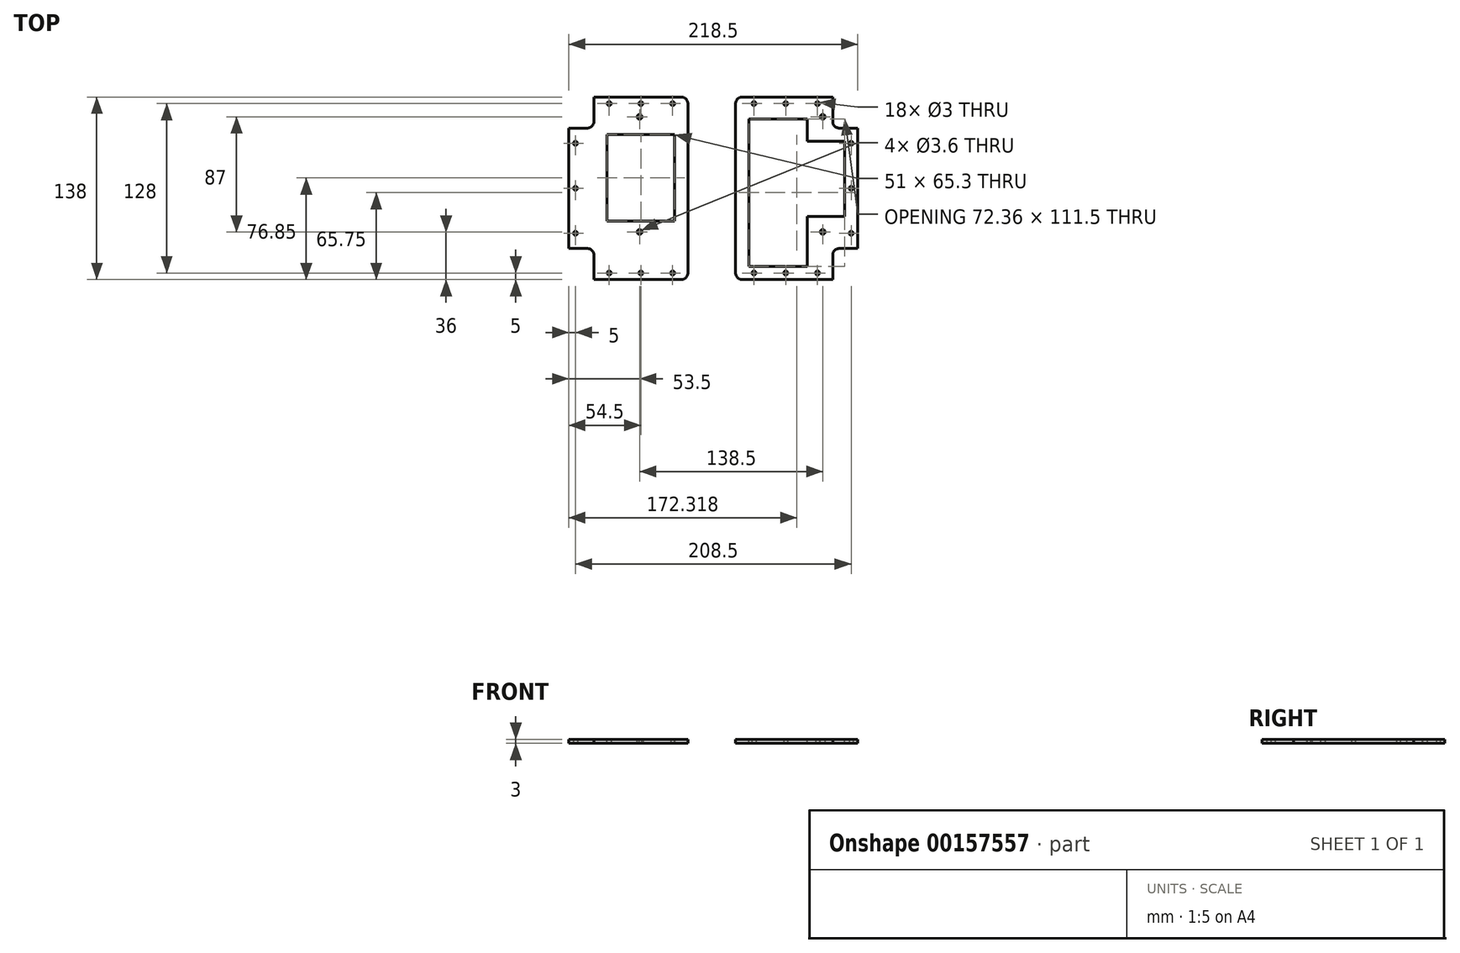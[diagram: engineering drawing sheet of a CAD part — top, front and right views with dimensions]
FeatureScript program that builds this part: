
annotation { "Feature Type Name" : "Feature", "Feature Type Description" : "" }
export const myFeature = defineFeature(function(context is Context, id is Id, definition is map)
    precondition{}
    {
        {
            var Q0;
            Q0=qCreatedBy(makeId("Top.planeOp"),FACE);
            var sketch = newSketch(context, id + "F0", { "sketchPlane" : qUnion([Q0])});
            skLineSegment(sketch, "E0.bottom", {"start": v(49.5, 64) * mm, "end": v(-49.5, 64) * mm, "construction": true});
            skLineSegment(sketch, "E0.top", {"start": v(49.5, -64) * mm, "end": v(-49.5, -64) * mm, "construction": true});
            skLineSegment(sketch, "E0.left", {"start": v(49.5, 64) * mm, "end": v(49.5, -64) * mm, "construction": true});
            skLineSegment(sketch, "E0.right", {"start": v(-49.5, 64) * mm, "end": v(-49.5, -64) * mm, "construction": true});
            skPoint(sketch, "E0.middle", {"position": v(0, 0) * mm});
            skCircle(sketch, "E1", {"center": v(-49.5, 0) * mm, "radius": 1.5 * mm});
            skCircle(sketch, "E2", {"center": v(-49.5, 34) * mm, "radius": 1.5 * mm});
            skCircle(sketch, "E3", {"center": v(-49.5, -34) * mm, "radius": 1.5 * mm});
            skCircle(sketch, "E4", {"center": v(-24, -64) * mm, "radius": 1.5 * mm});
            skCircle(sketch, "E5", {"center": v(0, -64) * mm, "radius": 1.5 * mm});
            skCircle(sketch, "E6", {"center": v(24, -64) * mm, "radius": 1.5 * mm});
            skCircle(sketch, "E7", {"center": v(0, 64) * mm, "radius": 1.5 * mm});
            skCircle(sketch, "E8", {"center": v(24, 64) * mm, "radius": 1.5 * mm});
            skCircle(sketch, "E9", {"center": v(-24, 64) * mm, "radius": 1.5 * mm});
            skLineSegment(sketch, "E10.bottom", {"start": v(-54.5, 69) * mm, "end": v(35.5, 69) * mm});
            skLineSegment(sketch, "E10.top", {"start": v(-54.5, -69) * mm, "end": v(35.5, -69) * mm});
            skLineSegment(sketch, "E10.left", {"start": v(-54.5, 69) * mm, "end": v(-54.5, -69) * mm});
            skLineSegment(sketch, "E10.right", {"start": v(35.5, 69) * mm, "end": v(35.5, -69) * mm});
            skLineSegment(sketch, "E11.bottom", {"start": v(60, 64) * mm, "end": v(159, 64) * mm, "construction": true});
            skLineSegment(sketch, "E11.top", {"start": v(60, -64) * mm, "end": v(159, -64) * mm, "construction": true});
            skLineSegment(sketch, "E11.left", {"start": v(60, 64) * mm, "end": v(60, -64) * mm, "construction": true});
            skLineSegment(sketch, "E11.right", {"start": v(159, 64) * mm, "end": v(159, -64) * mm, "construction": true});
            skCircle(sketch, "E12", {"center": v(85.5, 64) * mm, "radius": 1.5 * mm});
            skCircle(sketch, "E13", {"center": v(109.5, 64) * mm, "radius": 1.5 * mm});
            skCircle(sketch, "E14", {"center": v(133.5, 64) * mm, "radius": 1.5 * mm});
            skCircle(sketch, "E15", {"center": v(109.5, -64) * mm, "radius": 1.5 * mm});
            skCircle(sketch, "E16", {"center": v(133.5, -64) * mm, "radius": 1.5 * mm});
            skCircle(sketch, "E17", {"center": v(85.5, -64) * mm, "radius": 1.5 * mm});
            skCircle(sketch, "E18", {"center": v(159, 34) * mm, "radius": 1.5 * mm});
            skCircle(sketch, "E19", {"center": v(159, 0) * mm, "radius": 1.5 * mm});
            skCircle(sketch, "E20", {"center": v(159, -34) * mm, "radius": 1.5 * mm});
            skLineSegment(sketch, "E21.bottom", {"start": v(71.64, 69) * mm, "end": v(164, 69) * mm});
            skLineSegment(sketch, "E21.top", {"start": v(71.64, -69) * mm, "end": v(164, -69) * mm});
            skLineSegment(sketch, "E21.left", {"start": v(71.64, 69) * mm, "end": v(71.64, -69) * mm});
            skLineSegment(sketch, "E21.right", {"start": v(164, 69) * mm, "end": v(164, -69) * mm});
            skSolve(sketch);
        }
        {
            var Q0;
            Q0=makeQuery(id+"F0.imprint","IMPRINT",FACE,{"disambiguationData":[TD([[makeQuery(id+"F0.imprint","IMPRINT",EDGE,{"derivedFrom":sQuery(id+"F0.wireOp",EDGE,"E1")}),-1.0]])]});
            var Q1;
            Q1=makeQuery(id+"F0.imprint","IMPRINT",FACE,{"disambiguationData":[TD([[makeQuery(id+"F0.imprint","IMPRINT",EDGE,{"derivedFrom":sQuery(id+"F0.wireOp",EDGE,"E12")}),-1.0]])]});
            extrude(context, id + "F1", {"entities" : qUnion([Q0, Q1]), "depth" : 3 * mm});
        }
        {
            var Q0;
            Q0=makeQuery(id+"F1.opExtrude","CAP_FACE",FACE,{"disambiguationData":[OSD([sQuery(id+"F0.wireOp",EDGE,"E1"),sQuery(id+"F0.wireOp",EDGE,"E2"),sQuery(id+"F0.wireOp",EDGE,"E3"),sQuery(id+"F0.wireOp",EDGE,"E4"),sQuery(id+"F0.wireOp",EDGE,"E5"),sQuery(id+"F0.wireOp",EDGE,"E6"),sQuery(id+"F0.wireOp",EDGE,"E7"),sQuery(id+"F0.wireOp",EDGE,"E8"),sQuery(id+"F0.wireOp",EDGE,"E9"),sQuery(id+"F0.wireOp",EDGE,"E10.bottom"),sQuery(id+"F0.wireOp",EDGE,"E10.top"),sQuery(id+"F0.wireOp",EDGE,"E10.left"),sQuery(id+"F0.wireOp",EDGE,"E10.right")])],"isStart":false});
            var sketch = newSketch(context, id + "F2", { "sketchPlane" : qUnion([Q0])});
            skLineSegment(sketch, "E22.bottom", {"start": v(-57.57, 71.82) * mm, "end": v(-35.5, 71.82) * mm});
            skLineSegment(sketch, "E22.top", {"start": v(-57.57, 45.5) * mm, "end": v(-35.5, 45.5) * mm});
            skLineSegment(sketch, "E22.left", {"start": v(-57.57, 71.82) * mm, "end": v(-57.57, 45.5) * mm});
            skLineSegment(sketch, "E22.right", {"start": v(-35.5, 71.82) * mm, "end": v(-35.5, 45.5) * mm});
            skLineSegment(sketch, "E23.bottom", {"start": v(-60.22, -45.5) * mm, "end": v(-35.5, -45.5) * mm});
            skLineSegment(sketch, "E23.top", {"start": v(-60.22, -76.77) * mm, "end": v(-35.5, -76.77) * mm});
            skLineSegment(sketch, "E23.left", {"start": v(-60.22, -45.5) * mm, "end": v(-60.22, -76.77) * mm});
            skLineSegment(sketch, "E23.right", {"start": v(-35.5, -45.5) * mm, "end": v(-35.5, -76.77) * mm});
            skSolve(sketch);
        }
        {
            var Q0;
            Q0=makeQuery(id+"F2.imprint","IMPRINT",FACE,{"disambiguationData":[TD([[makeQuery(id+"F2.imprint","IMPRINT",EDGE,{"derivedFrom":sQuery(id+"F2.wireOp",EDGE,"VDgyCrDu-SPCL-fZ3l-5v9R-33bLlP5n6OBU.bottom")}),-1.0]])]});
            var Q1;
            {var subQ0=sQuery(id+"F2.wireOp",EDGE,"E22.right");var subQ1=sQuery(id+"F2.wireOp",EDGE,"E22.top");var subQ2=makeQuery(id+"F2.imprint","INTERSECT",VERTEX,{"derivedFrom":[subQ1,subQ0]});Q1=makeQuery(id+"F2.imprint","IMPRINT",FACE,{"disambiguationData":[TD([[makeQuery(id+"F2.imprint","IMPRINT",EDGE,{"disambiguationData":[TD([[subQ2,1.0]])],"derivedFrom":subQ1}),1.0]])]});}
            var Q2;
            {var subQ0=sQuery(id+"F2.wireOp",EDGE,"E23.right");var subQ1=sQuery(id+"F2.wireOp",EDGE,"E23.bottom");var subQ2=makeQuery(id+"F2.imprint","INTERSECT",VERTEX,{"derivedFrom":[subQ1,subQ0]});Q2=makeQuery(id+"F2.imprint","IMPRINT",FACE,{"disambiguationData":[TD([[makeQuery(id+"F2.imprint","IMPRINT",EDGE,{"disambiguationData":[TD([[subQ2,1.0]])],"derivedFrom":subQ1}),-1.0]])]});}
            extrude(context, id + "F3", {"entities" : qUnion([Q0, Q1, Q2]), "operationType" : NewBodyOperationType.REMOVE, "oppositeDirection" : true, "depth" : 25 * mm});
        }
        {
            var Q0;
            Q0=makeQuery(id+"F1.opExtrude","CAP_FACE",FACE,{"disambiguationData":[OSD([sQuery(id+"F0.wireOp",EDGE,"E12"),sQuery(id+"F0.wireOp",EDGE,"E13"),sQuery(id+"F0.wireOp",EDGE,"E14"),sQuery(id+"F0.wireOp",EDGE,"E15"),sQuery(id+"F0.wireOp",EDGE,"E16"),sQuery(id+"F0.wireOp",EDGE,"E17"),sQuery(id+"F0.wireOp",EDGE,"E18"),sQuery(id+"F0.wireOp",EDGE,"E19"),sQuery(id+"F0.wireOp",EDGE,"E20"),sQuery(id+"F0.wireOp",EDGE,"E21.bottom"),sQuery(id+"F0.wireOp",EDGE,"E21.top"),sQuery(id+"F0.wireOp",EDGE,"E21.left"),sQuery(id+"F0.wireOp",EDGE,"E21.right")])],"isStart":false});
            var sketch = newSketch(context, id + "F4", { "sketchPlane" : qUnion([Q0])});
            skLineSegment(sketch, "E24.bottom", {"start": v(145, 79.76) * mm, "end": v(176.38, 79.76) * mm});
            skLineSegment(sketch, "E24.top", {"start": v(145, 45.5) * mm, "end": v(176.38, 45.5) * mm});
            skLineSegment(sketch, "E24.left", {"start": v(145, 79.76) * mm, "end": v(145, 45.5) * mm});
            skLineSegment(sketch, "E24.right", {"start": v(176.38, 79.76) * mm, "end": v(176.38, 45.5) * mm});
            skLineSegment(sketch, "E25.bottom", {"start": v(145, -45.5) * mm, "end": v(181.26, -45.5) * mm});
            skLineSegment(sketch, "E25.top", {"start": v(145, -79.2) * mm, "end": v(181.26, -79.2) * mm});
            skLineSegment(sketch, "E25.left", {"start": v(145, -45.5) * mm, "end": v(145, -79.2) * mm});
            skLineSegment(sketch, "E25.right", {"start": v(181.26, -45.5) * mm, "end": v(181.26, -79.2) * mm});
            skSolve(sketch);
        }
        {
            var Q0;
            {var subQ0=sQuery(id+"F4.wireOp",EDGE,"E24.left");var subQ1=sQuery(id+"F4.wireOp",EDGE,"E24.top");var subQ2=makeQuery(id+"F4.imprint","INTERSECT",VERTEX,{"derivedFrom":[subQ1,subQ0]});Q0=makeQuery(id+"F4.imprint","IMPRINT",FACE,{"disambiguationData":[TD([[makeQuery(id+"F4.imprint","IMPRINT",EDGE,{"disambiguationData":[TD([[subQ2,-1.0]])],"derivedFrom":subQ1}),1.0]])]});}
            var Q1;
            {var subQ0=sQuery(id+"F4.wireOp",EDGE,"E25.left");var subQ1=sQuery(id+"F4.wireOp",EDGE,"E25.bottom");var subQ2=makeQuery(id+"F4.imprint","INTERSECT",VERTEX,{"derivedFrom":[subQ1,subQ0]});Q1=makeQuery(id+"F4.imprint","IMPRINT",FACE,{"disambiguationData":[TD([[makeQuery(id+"F4.imprint","IMPRINT",EDGE,{"disambiguationData":[TD([[subQ2,-1.0]])],"derivedFrom":subQ1}),-1.0]])]});}
            extrude(context, id + "F5", {"entities" : qUnion([Q0, Q1]), "operationType" : NewBodyOperationType.REMOVE, "oppositeDirection" : true, "depth" : 25 * mm});
        }
        {
            var Q0;
            Q0=makeQuery(id+"F3.boolean.opBoolean","COPY",EDGE,{"derivedFrom":makeQuery(id+"F3.opExtrude","SWEPT_EDGE",EDGE,{"disambiguationData":[OSD([sQuery(id+"F0.wireOp",EDGE,"E10.left"),sQuery(id+"F2.wireOp",EDGE,"E22.top")])]})});
            var Q1;
            Q1=makeQuery(id+"F3.boolean.opBoolean","COPY",EDGE,{"derivedFrom":makeQuery(id+"F3.opExtrude","SWEPT_EDGE",EDGE,{"disambiguationData":[OSD([sQuery(id+"F0.wireOp",EDGE,"E10.left"),sQuery(id+"F2.wireOp",EDGE,"E23.bottom")])]})});
            var Q2;
            Q2=makeQuery(id+"F3.boolean.opBoolean","COPY",EDGE,{"derivedFrom":makeQuery(id+"F3.opExtrude","SWEPT_EDGE",EDGE,{"disambiguationData":[OSD([sQuery(id+"F2.wireOp",EDGE,"E23.bottom"),sQuery(id+"F2.wireOp",EDGE,"E23.right")])]})});
            var Q3;
            Q3=makeQuery(id+"F3.boolean.opBoolean","COPY",EDGE,{"derivedFrom":makeQuery(id+"F3.opExtrude","SWEPT_EDGE",EDGE,{"disambiguationData":[OSD([sQuery(id+"F0.wireOp",EDGE,"E10.top"),sQuery(id+"F2.wireOp",EDGE,"E23.right")])]})});
            var Q4;
            Q4=makeQuery(id+"F1.opExtrude","SWEPT_EDGE",EDGE,{"disambiguationData":[OSD([sQuery(id+"F0.wireOp",EDGE,"E10.top"),sQuery(id+"F0.wireOp",EDGE,"E10.right")])]});
            var Q5;
            Q5=makeQuery(id+"F1.opExtrude","SWEPT_EDGE",EDGE,{"disambiguationData":[OSD([sQuery(id+"F0.wireOp",EDGE,"E10.bottom"),sQuery(id+"F0.wireOp",EDGE,"E10.right")])]});
            var Q6;
            Q6=makeQuery(id+"F3.boolean.opBoolean","COPY",EDGE,{"derivedFrom":makeQuery(id+"F3.opExtrude","SWEPT_EDGE",EDGE,{"disambiguationData":[OSD([sQuery(id+"F0.wireOp",EDGE,"E10.bottom"),sQuery(id+"F2.wireOp",EDGE,"E22.right")])]})});
            var Q7;
            Q7=makeQuery(id+"F3.boolean.opBoolean","COPY",EDGE,{"derivedFrom":makeQuery(id+"F3.opExtrude","SWEPT_EDGE",EDGE,{"disambiguationData":[OSD([sQuery(id+"F2.wireOp",EDGE,"E22.top"),sQuery(id+"F2.wireOp",EDGE,"E22.right")])]})});
            var Q8;
            Q8=makeQuery(id+"F3.boolean.opBoolean","COPY",EDGE,{"derivedFrom":makeQuery(id+"F3.opExtrude","SWEPT_EDGE",EDGE,{"disambiguationData":[OSD([sQuery(id+"F2.wireOp",EDGE,"VDgyCrDu-SPCL-fZ3l-5v9R-33bLlP5n6OBU.bottom"),sQuery(id+"F2.wireOp",EDGE,"VDgyCrDu-SPCL-fZ3l-5v9R-33bLlP5n6OBU.left")])]})});
            var Q9;
            Q9=makeQuery(id+"F3.boolean.opBoolean","COPY",EDGE,{"derivedFrom":makeQuery(id+"F3.opExtrude","SWEPT_EDGE",EDGE,{"disambiguationData":[OSD([sQuery(id+"F2.wireOp",EDGE,"VDgyCrDu-SPCL-fZ3l-5v9R-33bLlP5n6OBU.bottom"),sQuery(id+"F2.wireOp",EDGE,"VDgyCrDu-SPCL-fZ3l-5v9R-33bLlP5n6OBU.right")])]})});
            var Q10;
            Q10=makeQuery(id+"F3.boolean.opBoolean","COPY",EDGE,{"derivedFrom":makeQuery(id+"F3.opExtrude","SWEPT_EDGE",EDGE,{"disambiguationData":[OSD([sQuery(id+"F2.wireOp",EDGE,"VDgyCrDu-SPCL-fZ3l-5v9R-33bLlP5n6OBU.top"),sQuery(id+"F2.wireOp",EDGE,"VDgyCrDu-SPCL-fZ3l-5v9R-33bLlP5n6OBU.right")])]})});
            var Q11;
            Q11=makeQuery(id+"F3.boolean.opBoolean","COPY",EDGE,{"derivedFrom":makeQuery(id+"F3.opExtrude","SWEPT_EDGE",EDGE,{"disambiguationData":[OSD([sQuery(id+"F2.wireOp",EDGE,"VDgyCrDu-SPCL-fZ3l-5v9R-33bLlP5n6OBU.top"),sQuery(id+"F2.wireOp",EDGE,"VDgyCrDu-SPCL-fZ3l-5v9R-33bLlP5n6OBU.left")])]})});
            var Q12;
            Q12=makeQuery(id+"F1.opExtrude","SWEPT_EDGE",EDGE,{"disambiguationData":[OSD([sQuery(id+"F0.wireOp",EDGE,"E21.bottom"),sQuery(id+"F0.wireOp",EDGE,"E21.left")])]});
            var Q13;
            Q13=makeQuery(id+"F5.boolean.opBoolean","COPY",EDGE,{"derivedFrom":makeQuery(id+"F5.opExtrude","SWEPT_EDGE",EDGE,{"disambiguationData":[OSD([sQuery(id+"F0.wireOp",EDGE,"E21.bottom"),sQuery(id+"F4.wireOp",EDGE,"E24.left")])]})});
            var Q14;
            Q14=makeQuery(id+"F5.boolean.opBoolean","COPY",EDGE,{"derivedFrom":makeQuery(id+"F5.opExtrude","SWEPT_EDGE",EDGE,{"disambiguationData":[OSD([sQuery(id+"F4.wireOp",EDGE,"E24.top"),sQuery(id+"F4.wireOp",EDGE,"E24.left")])]})});
            var Q15;
            Q15=makeQuery(id+"F5.boolean.opBoolean","COPY",EDGE,{"derivedFrom":makeQuery(id+"F5.opExtrude","SWEPT_EDGE",EDGE,{"disambiguationData":[OSD([sQuery(id+"F0.wireOp",EDGE,"E21.right"),sQuery(id+"F4.wireOp",EDGE,"E24.top")])]})});
            var Q16;
            Q16=makeQuery(id+"F5.boolean.opBoolean","COPY",EDGE,{"derivedFrom":makeQuery(id+"F5.opExtrude","SWEPT_EDGE",EDGE,{"disambiguationData":[OSD([sQuery(id+"F0.wireOp",EDGE,"E21.right"),sQuery(id+"F4.wireOp",EDGE,"E25.bottom")])]})});
            var Q17;
            Q17=makeQuery(id+"F5.boolean.opBoolean","COPY",EDGE,{"derivedFrom":makeQuery(id+"F5.opExtrude","SWEPT_EDGE",EDGE,{"disambiguationData":[OSD([sQuery(id+"F4.wireOp",EDGE,"E25.bottom"),sQuery(id+"F4.wireOp",EDGE,"E25.left")])]})});
            var Q18;
            Q18=makeQuery(id+"F5.boolean.opBoolean","COPY",EDGE,{"derivedFrom":makeQuery(id+"F5.opExtrude","SWEPT_EDGE",EDGE,{"disambiguationData":[OSD([sQuery(id+"F0.wireOp",EDGE,"E21.top"),sQuery(id+"F4.wireOp",EDGE,"E25.left")])]})});
            var Q19;
            Q19=makeQuery(id+"F1.opExtrude","SWEPT_EDGE",EDGE,{"disambiguationData":[OSD([sQuery(id+"F0.wireOp",EDGE,"E21.top"),sQuery(id+"F0.wireOp",EDGE,"E21.left")])]});
            fillet(context, id + "F6", {"entities" : qUnion([Q0, Q1, Q2, Q3, Q4, Q5, Q6, Q7, Q8, Q9, Q10, Q11, Q12, Q13, Q14, Q15, Q16, Q17, Q18, Q19]), "radius" : 5 * mm, "tangentPropagation" : true, "allowEdgeOverflow" : false});
        }
        {
            var Q0;
            Q0=makeQuery(id+"F1.opExtrude","CAP_FACE",FACE,{"disambiguationData":[OSD([sQuery(id+"F0.wireOp",EDGE,"E1"),sQuery(id+"F0.wireOp",EDGE,"E2"),sQuery(id+"F0.wireOp",EDGE,"E3"),sQuery(id+"F0.wireOp",EDGE,"E4"),sQuery(id+"F0.wireOp",EDGE,"E5"),sQuery(id+"F0.wireOp",EDGE,"E6"),sQuery(id+"F0.wireOp",EDGE,"E7"),sQuery(id+"F0.wireOp",EDGE,"E8"),sQuery(id+"F0.wireOp",EDGE,"E9"),sQuery(id+"F0.wireOp",EDGE,"E10.bottom"),sQuery(id+"F0.wireOp",EDGE,"E10.top"),sQuery(id+"F0.wireOp",EDGE,"E10.left"),sQuery(id+"F0.wireOp",EDGE,"E10.right")])],"isStart":false});
            var sketch = newSketch(context, id + "F7", { "sketchPlane" : qUnion([Q0])});
            skLineSegment(sketch, "E26.bottom", {"start": v(-1, 54) * mm, "end": v(137.5, 54) * mm, "construction": true});
            skLineSegment(sketch, "E26.top", {"start": v(-1, -33) * mm, "end": v(137.5, -33) * mm, "construction": true});
            skLineSegment(sketch, "E26.left", {"start": v(-1, 54) * mm, "end": v(-1, -33) * mm, "construction": true});
            skLineSegment(sketch, "E26.right", {"start": v(137.5, 54) * mm, "end": v(137.5, -33) * mm, "construction": true});
            skCircle(sketch, "E27", {"center": v(137.5, -33) * mm, "radius": 1.8 * mm});
            skCircle(sketch, "E28", {"center": v(137.5, 54) * mm, "radius": 1.8 * mm});
            skCircle(sketch, "E29", {"center": v(-1, 54) * mm, "radius": 1.8 * mm});
            skCircle(sketch, "E30", {"center": v(-1, -33) * mm, "radius": 1.8 * mm});
            skSolve(sketch);
        }
        {
            var Q0;
            Q0=makeQuery(id+"F7.imprint","IMPRINT",FACE,{"disambiguationData":[TD([[makeQuery(id+"F7.imprint","IMPRINT",EDGE,{"derivedFrom":sQuery(id+"F7.wireOp",EDGE,"E29")}),1.0]])]});
            var Q1;
            Q1=makeQuery(id+"F7.imprint","IMPRINT",FACE,{"disambiguationData":[TD([[makeQuery(id+"F7.imprint","IMPRINT",EDGE,{"derivedFrom":sQuery(id+"F7.wireOp",EDGE,"E30")}),1.0]])]});
            var Q2;
            Q2=makeQuery(id+"F7.imprint","IMPRINT",FACE,{"disambiguationData":[TD([[makeQuery(id+"F7.imprint","IMPRINT",EDGE,{"derivedFrom":sQuery(id+"F7.wireOp",EDGE,"E27")}),1.0]])]});
            var Q3;
            Q3=makeQuery(id+"F7.imprint","IMPRINT",FACE,{"disambiguationData":[TD([[makeQuery(id+"F7.imprint","IMPRINT",EDGE,{"derivedFrom":sQuery(id+"F7.wireOp",EDGE,"E28")}),1.0]])]});
            extrude(context, id + "F8", {"entities" : qUnion([Q0, Q1, Q2, Q3]), "operationType" : NewBodyOperationType.REMOVE, "oppositeDirection" : true, "depth" : 25 * mm});
        }
        {
            var Q0;
            Q0=makeQuery(id+"F1.opExtrude","CAP_FACE",FACE,{"disambiguationData":[OSD([sQuery(id+"F0.wireOp",EDGE,"E12"),sQuery(id+"F0.wireOp",EDGE,"E13"),sQuery(id+"F0.wireOp",EDGE,"E14"),sQuery(id+"F0.wireOp",EDGE,"E15"),sQuery(id+"F0.wireOp",EDGE,"E16"),sQuery(id+"F0.wireOp",EDGE,"E17"),sQuery(id+"F0.wireOp",EDGE,"E18"),sQuery(id+"F0.wireOp",EDGE,"E19"),sQuery(id+"F0.wireOp",EDGE,"E20"),sQuery(id+"F0.wireOp",EDGE,"E21.bottom"),sQuery(id+"F0.wireOp",EDGE,"E21.top"),sQuery(id+"F0.wireOp",EDGE,"E21.left"),sQuery(id+"F0.wireOp",EDGE,"E21.right")])],"isStart":false});
            var sketch = newSketch(context, id + "F9", { "sketchPlane" : qUnion([Q0])});
            skLineSegment(sketch, "E31.bottom", {"start": v(81.64, 52.5) * mm, "end": v(125.7, 52.5) * mm});
            skLineSegment(sketch, "E31.top", {"start": v(81.64, -59) * mm, "end": v(125.7, -59) * mm});
            skLineSegment(sketch, "E31.left", {"start": v(81.64, 52.5) * mm, "end": v(81.64, -59) * mm});
            skLineSegment(sketch, "E31.right", {"start": v(125.7, 52.5) * mm, "end": v(125.7, -59) * mm});
            skLineSegment(sketch, "E32.bottom", {"start": v(125.7, 35.5) * mm, "end": v(154, 35.5) * mm});
            skLineSegment(sketch, "E32.top", {"start": v(125.7, -21.2) * mm, "end": v(154, -21.2) * mm});
            skLineSegment(sketch, "E32.left", {"start": v(125.7, 35.5) * mm, "end": v(125.7, -21.2) * mm});
            skLineSegment(sketch, "E32.right", {"start": v(154, 35.5) * mm, "end": v(154, -21.2) * mm});
            skSolve(sketch);
        }
        {
            var Q0;
            {var subQ1=sQuery(id+"F9.wireOp",EDGE,"E31.bottom");Q0=makeQuery(id+"F9.imprint","IMPRINT",FACE,{"disambiguationData":[TD([[makeQuery(id+"F9.imprint","IMPRINT",EDGE,{"derivedFrom":subQ1}),-1.0]])]});}
            var Q1;
            Q1=makeQuery(id+"F9.imprint","IMPRINT",FACE,{"disambiguationData":[TD([[makeQuery(id+"F9.imprint","IMPRINT",EDGE,{"derivedFrom":sQuery(id+"F9.wireOp",EDGE,"E32.bottom")}),-1.0]])]});
            var Q2;
            Q2=makeQuery(id+"F11.imprint","IMPRINT",FACE,{"disambiguationData":[TD([[makeQuery(id+"F11.imprint","IMPRINT",EDGE,{"derivedFrom":sQuery(id+"F11.wireOp",EDGE,"E33.bottom")}),-1.0]])]});
            extrude(context, id + "F10", {"entities" : qUnion([Q0, Q1, Q2]), "operationType" : NewBodyOperationType.REMOVE, "oppositeDirection" : true, "depth" : 25 * mm});
        }
        {
            var Q0;
            Q0=makeQuery(id+"F1.opExtrude","CAP_FACE",FACE,{"disambiguationData":[OSD([sQuery(id+"F0.wireOp",EDGE,"E1"),sQuery(id+"F0.wireOp",EDGE,"E2"),sQuery(id+"F0.wireOp",EDGE,"E3"),sQuery(id+"F0.wireOp",EDGE,"E4"),sQuery(id+"F0.wireOp",EDGE,"E5"),sQuery(id+"F0.wireOp",EDGE,"E6"),sQuery(id+"F0.wireOp",EDGE,"E7"),sQuery(id+"F0.wireOp",EDGE,"E8"),sQuery(id+"F0.wireOp",EDGE,"E9"),sQuery(id+"F0.wireOp",EDGE,"E10.bottom"),sQuery(id+"F0.wireOp",EDGE,"E10.top"),sQuery(id+"F0.wireOp",EDGE,"E10.left"),sQuery(id+"F0.wireOp",EDGE,"E10.right")])],"isStart":false});
            var sketch = newSketch(context, id + "F11", { "sketchPlane" : qUnion([Q0])});
            skLineSegment(sketch, "E33.bottom", {"start": v(-25.5, 40.5) * mm, "end": v(25.5, 40.5) * mm});
            skLineSegment(sketch, "E33.top", {"start": v(-25.5, -24.8) * mm, "end": v(25.5, -24.8) * mm});
            skLineSegment(sketch, "E33.left", {"start": v(-25.5, 40.5) * mm, "end": v(-25.5, -24.8) * mm});
            skLineSegment(sketch, "E33.right", {"start": v(25.5, 40.5) * mm, "end": v(25.5, -24.8) * mm});
            skSolve(sketch);
        }
        {
            var Q0;
            Q0=makeQuery(id+"F11.imprint","IMPRINT",FACE,{"disambiguationData":[TD([[makeQuery(id+"F11.imprint","IMPRINT",EDGE,{"derivedFrom":sQuery(id+"F11.wireOp",EDGE,"E33.bottom")}),-1.0]])]});
            extrude(context, id + "F12", {"entities" : qUnion([Q0]), "operationType" : NewBodyOperationType.REMOVE, "oppositeDirection" : true, "depth" : 25 * mm});
        }
    });
